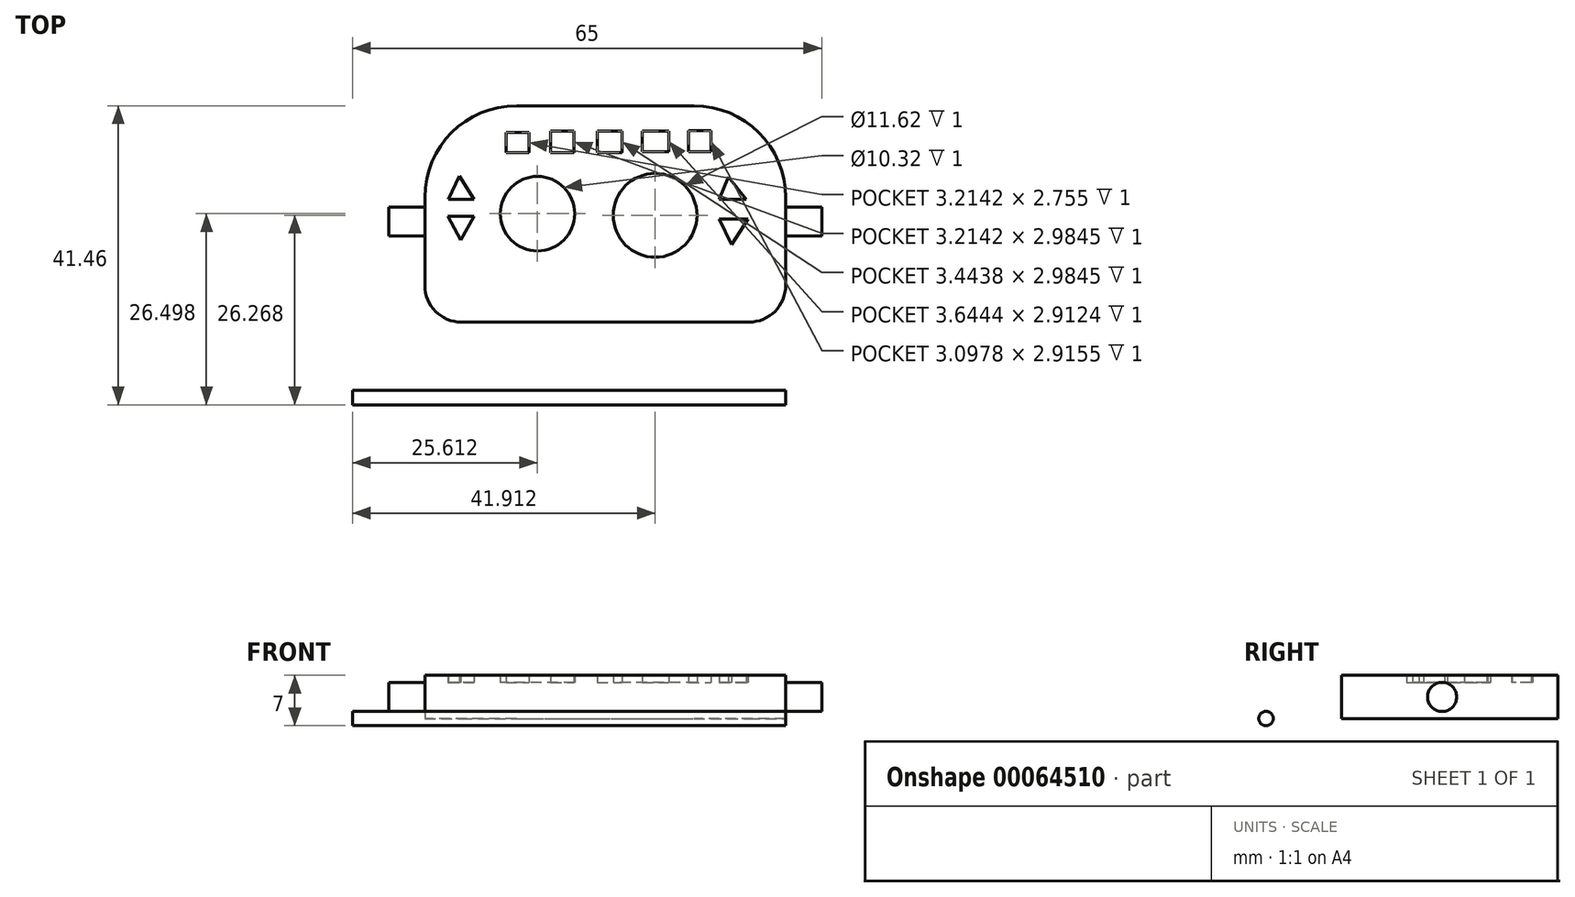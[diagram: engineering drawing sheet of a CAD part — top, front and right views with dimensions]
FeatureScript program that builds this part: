
annotation { "Feature Type Name" : "Feature", "Feature Type Description" : "" }
export const myFeature = defineFeature(function(context is Context, id is Id, definition is map)
    precondition{}
    {
        {
            var Q0;
            Q0=qCreatedBy(makeId("Top.planeOp"),FACE);
            var sketch = newSketch(context, id + "F0", { "sketchPlane" : qUnion([Q0])});
            skLineSegment(sketch, "E0.bottom", {"start": v(0, 0) * mm, "end": v(50, 0) * mm});
            skLineSegment(sketch, "E0.top", {"start": v(0, 30) * mm, "end": v(50, 30) * mm});
            skLineSegment(sketch, "E0.left", {"start": v(0, 0) * mm, "end": v(0, 30) * mm});
            skLineSegment(sketch, "E0.right", {"start": v(50, 0) * mm, "end": v(50, 30) * mm});
            skSolve(sketch);
        }
        {
            var Q0;
            Q0=makeQuery(id+"F0.imprint","IMPRINT",FACE,{"disambiguationData":[TD([[makeQuery(id+"F0.imprint","IMPRINT",EDGE,{"derivedFrom":sQuery(id+"F0.wireOp",EDGE,"E0.bottom")}),1.0]])]});
            extrude(context, id + "F1", {"entities" : qUnion([Q0]), "depth" : 5 * mm});
        }
        {
            var Q0;
            Q0=makeQuery(id+"F1.opExtrude","SWEPT_EDGE",EDGE,{"disambiguationData":[OSD([sQuery(id+"F0.wireOp",EDGE,"E0.top"),sQuery(id+"F0.wireOp",EDGE,"E0.left")])]});
            fillet(context, id + "F2", {"entities" : qUnion([Q0]), "radius" : 12.7 * mm, "tangentPropagation" : true, "allowEdgeOverflow" : false});
        }
        {
            var Q0;
            Q0=makeQuery(id+"F1.opExtrude","SWEPT_EDGE",EDGE,{"disambiguationData":[OSD([sQuery(id+"F0.wireOp",EDGE,"E0.top"),sQuery(id+"F0.wireOp",EDGE,"E0.right")])]});
            fillet(context, id + "F3", {"entities" : qUnion([Q0]), "radius" : 12.7 * mm, "tangentPropagation" : true, "allowEdgeOverflow" : false});
        }
        {
            var Q0;
            Q0=makeQuery(id+"F1.opExtrude","SWEPT_EDGE",EDGE,{"disambiguationData":[OSD([sQuery(id+"F0.wireOp",EDGE,"E0.bottom"),sQuery(id+"F0.wireOp",EDGE,"E0.left")])]});
            fillet(context, id + "F4", {"entities" : qUnion([Q0]), "radius" : 5.08 * mm, "tangentPropagation" : true, "allowEdgeOverflow" : false});
        }
        {
            var Q0;
            Q0=makeQuery(id+"F1.opExtrude","SWEPT_EDGE",EDGE,{"disambiguationData":[OSD([sQuery(id+"F0.wireOp",EDGE,"E0.bottom"),sQuery(id+"F0.wireOp",EDGE,"E0.right")])]});
            fillet(context, id + "F5", {"entities" : qUnion([Q0]), "radius" : 5.08 * mm, "tangentPropagation" : true, "allowEdgeOverflow" : false});
        }
        {
            var Q0;
            Q0=makeQuery(id+"F1.opExtrude","CAP_FACE",FACE,{"disambiguationData":[OSD([sQuery(id+"F0.wireOp",EDGE,"E0.bottom"),sQuery(id+"F0.wireOp",EDGE,"E0.top"),sQuery(id+"F0.wireOp",EDGE,"E0.left"),sQuery(id+"F0.wireOp",EDGE,"E0.right")])],"isStart":false});
            var sketch = newSketch(context, id + "F6", { "sketchPlane" : qUnion([Q0])});
            skCircle(sketch, "E1", {"center": v(15.61, 15.04) * mm, "radius": 5.16 * mm});
            skCircle(sketch, "E2", {"center": v(31.91, 14.8) * mm, "radius": 5.8 * mm});
            skLineSegment(sketch, "E3.bottom", {"start": v(11.25, 26.29) * mm, "end": v(14.46, 26.29) * mm});
            skLineSegment(sketch, "E3.top", {"start": v(11.25, 23.53) * mm, "end": v(14.46, 23.53) * mm});
            skLineSegment(sketch, "E3.left", {"start": v(11.25, 26.29) * mm, "end": v(11.25, 23.53) * mm});
            skLineSegment(sketch, "E3.right", {"start": v(14.46, 26.29) * mm, "end": v(14.46, 23.53) * mm});
            skLineSegment(sketch, "E4.bottom", {"start": v(17.45, 26.52) * mm, "end": v(20.66, 26.52) * mm});
            skLineSegment(sketch, "E4.top", {"start": v(17.45, 23.53) * mm, "end": v(20.66, 23.53) * mm});
            skLineSegment(sketch, "E4.left", {"start": v(17.45, 26.52) * mm, "end": v(17.45, 23.53) * mm});
            skLineSegment(sketch, "E4.right", {"start": v(20.66, 26.52) * mm, "end": v(20.66, 23.53) * mm});
            skLineSegment(sketch, "E5.bottom", {"start": v(23.88, 26.52) * mm, "end": v(27.32, 26.52) * mm});
            skLineSegment(sketch, "E5.top", {"start": v(23.88, 23.53) * mm, "end": v(27.32, 23.53) * mm});
            skLineSegment(sketch, "E5.left", {"start": v(23.88, 26.52) * mm, "end": v(23.88, 23.53) * mm});
            skLineSegment(sketch, "E5.right", {"start": v(27.32, 26.52) * mm, "end": v(27.32, 23.53) * mm});
            skPoint(sketch, "E6.firstSnap0", {"position": v(19.06, 26.52) * mm});
            skLineSegment(sketch, "E6.bottom", {"start": v(30.14, 26.52) * mm, "end": v(33.79, 26.52) * mm});
            skLineSegment(sketch, "E6.top", {"start": v(30.14, 23.6) * mm, "end": v(33.79, 23.6) * mm});
            skLineSegment(sketch, "E6.left", {"start": v(30.14, 26.52) * mm, "end": v(30.14, 23.6) * mm});
            skLineSegment(sketch, "E6.right", {"start": v(33.79, 26.52) * mm, "end": v(33.79, 23.6) * mm});
            skLineSegment(sketch, "E7.bottom", {"start": v(36.52, 26.52) * mm, "end": v(39.62, 26.52) * mm});
            skLineSegment(sketch, "E7.top", {"start": v(36.52, 23.6) * mm, "end": v(39.62, 23.6) * mm});
            skLineSegment(sketch, "E7.left", {"start": v(36.52, 26.52) * mm, "end": v(36.52, 23.6) * mm});
            skLineSegment(sketch, "E7.right", {"start": v(39.62, 26.52) * mm, "end": v(39.62, 23.6) * mm});
            skLineSegment(sketch, "E8", {"start": v(4.82, 20.23) * mm, "end": v(3.27, 17.04) * mm});
            skLineSegment(sketch, "E9", {"start": v(3.27, 17.04) * mm, "end": v(6.82, 17.04) * mm});
            skLineSegment(sketch, "E10", {"start": v(6.82, 17.04) * mm, "end": v(4.82, 20.23) * mm});
            skLineSegment(sketch, "E11", {"start": v(3.18, 14.68) * mm, "end": v(6.82, 14.68) * mm});
            skLineSegment(sketch, "E12", {"start": v(6.82, 14.68) * mm, "end": v(5, 11.4) * mm});
            skLineSegment(sketch, "E13", {"start": v(5, 11.4) * mm, "end": v(3.18, 14.68) * mm});
            skLineSegment(sketch, "E14", {"start": v(40.8, 17.04) * mm, "end": v(44.54, 17.04) * mm});
            skLineSegment(sketch, "E15", {"start": v(44.54, 17.04) * mm, "end": v(42.08, 20.14) * mm});
            skLineSegment(sketch, "E16", {"start": v(42.08, 20.14) * mm, "end": v(40.8, 17.04) * mm});
            skLineSegment(sketch, "E17", {"start": v(40.8, 14.31) * mm, "end": v(44.81, 14.31) * mm});
            skLineSegment(sketch, "E18", {"start": v(44.81, 14.31) * mm, "end": v(42.54, 10.76) * mm});
            skLineSegment(sketch, "E19", {"start": v(42.54, 10.76) * mm, "end": v(40.8, 14.31) * mm});
            skSolve(sketch);
        }
        {
            var Q0;
            Q0=makeQuery(id+"F6.imprint","IMPRINT",FACE,{"disambiguationData":[TD([[makeQuery(id+"F6.imprint","IMPRINT",EDGE,{"derivedFrom":sQuery(id+"F6.wireOp",EDGE,"E1")}),-1.0]])]});
            extrude(context, id + "F7", {"entities" : qUnion([Q0]), "operationType" : NewBodyOperationType.ADD, "depth" : 1 * mm});
        }
        {
            var Q0;
            {var subQ0=sQuery(id+"F0.wireOp",EDGE,"E0.left");Q0=makeQuery(id+"F7.boolean.opBoolean","MERGE",FACE,{"derivedFrom":[makeQuery(id+"F1.opExtrude","SWEPT_FACE",FACE,{"disambiguationData":[OSD([subQ0])]}),makeQuery(id+"F7.opExtrude","SWEPT_FACE",FACE,{"disambiguationData":[OSD([subQ0])]})]});}
            var sketch = newSketch(context, id + "F8", { "sketchPlane" : qUnion([Q0])});
            skCircle(sketch, "E20", {"center": v(-13.96, 3) * mm, "radius": 2 * mm});
            skPoint(sketch, "E20.centerSnap0", {"position": v(-17.3, 3) * mm});
            skSolve(sketch);
        }
        {
            var Q0;
            Q0=makeQuery(id+"F8.imprint","IMPRINT",FACE,{"disambiguationData":[TD([[makeQuery(id+"F8.imprint","IMPRINT",EDGE,{"derivedFrom":sQuery(id+"F8.wireOp",EDGE,"E20")}),1.0]])]});
            extrude(context, id + "F9", {"entities" : qUnion([Q0]), "operationType" : NewBodyOperationType.ADD, "depth" : 5 * mm});
        }
        {
            var Q0;
            {var subQ0=sQuery(id+"F0.wireOp",EDGE,"E0.right");Q0=makeQuery(id+"F7.boolean.opBoolean","MERGE",FACE,{"derivedFrom":[makeQuery(id+"F1.opExtrude","SWEPT_FACE",FACE,{"disambiguationData":[OSD([subQ0])]}),makeQuery(id+"F7.opExtrude","SWEPT_FACE",FACE,{"disambiguationData":[OSD([subQ0])]})]});}
            cPlane(context, id + "F10", {"entities" : qUnion([Q0]), "cplaneType" : CPlaneType.OFFSET, "offset" : 0 * mm, "width" : 152.4 * mm, "height" : 152.4 * mm});
        }
        {
            var Q0;
            Q0=qCreatedBy(id+"F10.planeOp",FACE);
            var sketch = newSketch(context, id + "F11", { "sketchPlane" : qUnion([Q0])});
            skCircle(sketch, "E21", {"center": v(13.94, 3) * mm, "radius": 2.01 * mm});
            skSolve(sketch);
        }
        {
            var Q0;
            Q0=makeQuery(id+"F11.imprint","IMPRINT",FACE,{"disambiguationData":[TD([[makeQuery(id+"F11.imprint","IMPRINT",EDGE,{"derivedFrom":sQuery(id+"F11.wireOp",EDGE,"E21")}),1.0]])]});
            extrude(context, id + "F12", {"entities" : qUnion([Q0]), "operationType" : NewBodyOperationType.ADD, "depth" : 5 * mm});
        }
        {
            var Q0;
            Q0=qCreatedBy(id+"F10.planeOp",FACE);
            var sketch = newSketch(context, id + "F13", { "sketchPlane" : qUnion([Q0])});
            skCircle(sketch, "E22", {"center": v(-10.46, 0) * mm, "radius": 1 * mm});
            skSolve(sketch);
        }
        {
            var Q0;
            Q0=qCreatedBy(makeId("Top.planeOp"),FACE);
            var sketch = newSketch(context, id + "F14", { "sketchPlane" : qUnion([Q0])});
            skLineSegment(sketch, "E23", {"start": v(49.93, -10.44) * mm, "end": v(-10.07, -10.44) * mm});
            skSolve(sketch);
        }
        {
            var Q0;
            Q0=makeQuery(id+"F13.imprint","IMPRINT",FACE,{"disambiguationData":[TD([[makeQuery(id+"F13.imprint","IMPRINT",EDGE,{"derivedFrom":sQuery(id+"F13.wireOp",EDGE,"E22")}),1.0]])]});
            var Q1;
            Q1=sQuery(id+"F14.wireOp",EDGE,"E23");
            sweep(context, id + "F15", {"profiles" : qUnion([Q0]), "path" : qUnion([Q1])});
        }
    });
